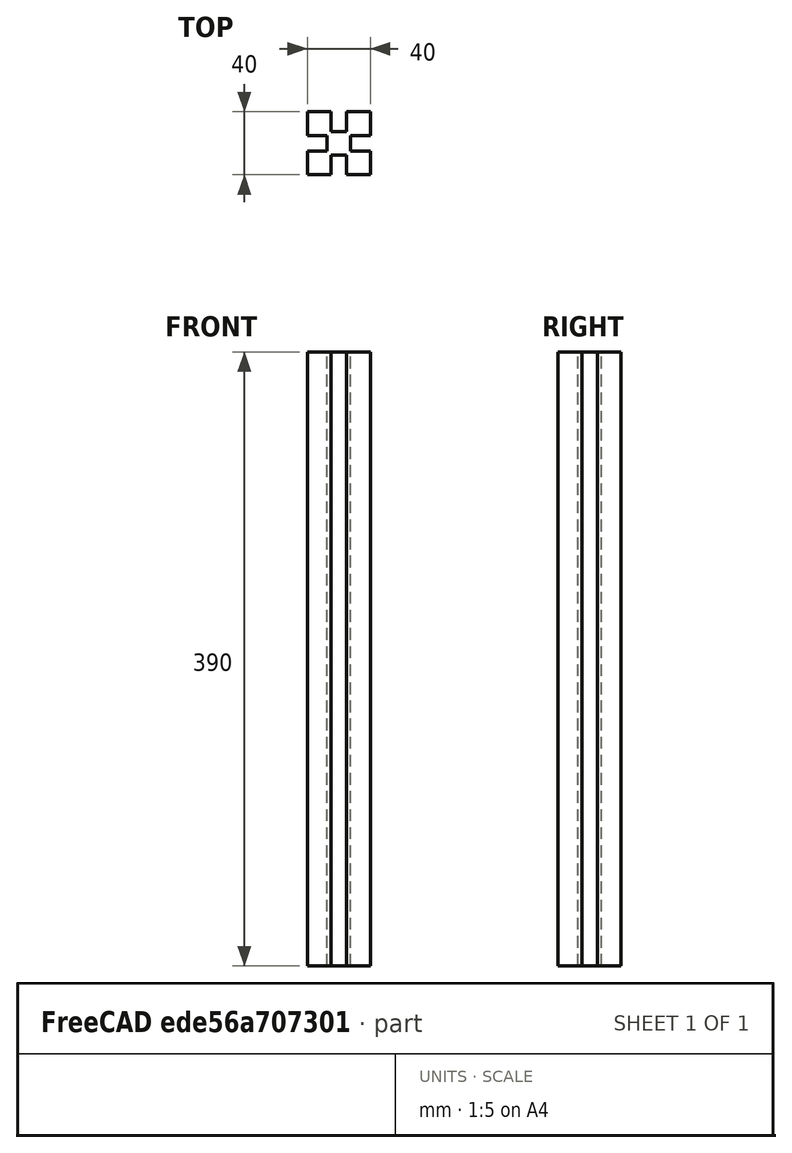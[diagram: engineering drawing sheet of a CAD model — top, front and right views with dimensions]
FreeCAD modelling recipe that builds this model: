
FCSTD DOCUMENT  (FreeCAD 0.18R14555 (Git shallow))
Label: t-slot-profile-390
License: All rights reserved
LicenseURL: http://en.wikipedia.org/wiki/All_rights_reserved
objects: Sketcher::SketchObject×1, PartDesign::Pad×1, PartDesign::Body×1
note: 4 computed .brp shape members not serialized (recipe doc carries the construction recipe); baked Part::Feature solids carry a one-line shape summary decoded from their .brp

FEATURE [Sketcher::SketchObject] Sketch
  MapMode = 5
  Support = -> [XY_Plane]
  sketch-geometry (30):
    g0: LineSegment StartX=-20 StartY=-20 StartZ=0 EndX=-20 EndY=-5 EndZ=0
    g1: LineSegment StartX=-20 StartY=-5 StartZ=0 EndX=-7.5 EndY=-5 EndZ=0
    g2: LineSegment StartX=-7.5 StartY=-5 StartZ=0 EndX=-7.5 EndY=5 EndZ=0
    g3: LineSegment StartX=-7.5 StartY=5 StartZ=0 EndX=-20 EndY=5 EndZ=0
    g4: LineSegment StartX=-20 StartY=5 StartZ=0 EndX=-20 EndY=20 EndZ=0
    g5: LineSegment StartX=-20 StartY=20 StartZ=0 EndX=-5 EndY=20 EndZ=0
    g6: LineSegment StartX=-5 StartY=20 StartZ=0 EndX=-5 EndY=7.5 EndZ=0
    g7: LineSegment StartX=-5 StartY=7.5 StartZ=0 EndX=5 EndY=7.5 EndZ=0
    g8: LineSegment StartX=5 StartY=7.5 StartZ=0 EndX=5 EndY=20 EndZ=0
    g9: LineSegment StartX=5 StartY=20 StartZ=0 EndX=20 EndY=20 EndZ=0
    g10: LineSegment StartX=20 StartY=20 StartZ=0 EndX=20 EndY=5 EndZ=0
    g11: LineSegment StartX=20 StartY=5 StartZ=0 EndX=7.5 EndY=5 EndZ=0
    g12: LineSegment StartX=7.5 StartY=5 StartZ=0 EndX=7.5 EndY=-5 EndZ=0
    g13: LineSegment StartX=7.5 StartY=-5 StartZ=0 EndX=20 EndY=-5 EndZ=0
    g14: LineSegment StartX=20 StartY=-5 StartZ=0 EndX=20 EndY=-20 EndZ=0
    g15: LineSegment StartX=20 StartY=-20 StartZ=0 EndX=5 EndY=-20 EndZ=0
    g16: LineSegment StartX=5 StartY=-20 StartZ=0 EndX=5 EndY=-7.5 EndZ=0
    g17: LineSegment StartX=5 StartY=-7.5 StartZ=0 EndX=-5 EndY=-7.5 EndZ=0
    g18: LineSegment StartX=-5 StartY=-7.5 StartZ=0 EndX=-5 EndY=-20 EndZ=0
    g19: LineSegment StartX=-5 StartY=-20 StartZ=0 EndX=-20 EndY=-20 EndZ=0
    g20: LineSegment [constr] StartX=-5 StartY=-7.5 StartZ=0 EndX=-5 EndY=7.5 EndZ=0
    g21: LineSegment [constr] StartX=5 StartY=7.5 StartZ=0 EndX=5 EndY=-7.5 EndZ=0
    g22: LineSegment [constr] StartX=-7.5 StartY=5 StartZ=0 EndX=7.5 EndY=5 EndZ=0
    g23: LineSegment [constr] StartX=7.5 StartY=-5 StartZ=0 EndX=-7.5 EndY=-5 EndZ=0
    g24: LineSegment [constr] StartX=-20 StartY=-5 StartZ=0 EndX=-20 EndY=5 EndZ=0
    g25: LineSegment [constr] StartX=-5 StartY=20 StartZ=0 EndX=5 EndY=20 EndZ=0
    g26: LineSegment [constr] StartX=20 StartY=5 StartZ=0 EndX=20 EndY=-5 EndZ=0
    g27: LineSegment [constr] StartX=-5 StartY=-20 StartZ=0 EndX=5 EndY=-20 EndZ=0
    g28: LineSegment [constr] StartX=20 StartY=-20 StartZ=0 EndX=-20 EndY=20 EndZ=0
    g29: LineSegment [constr] StartX=-20 StartY=-20 StartZ=0 EndX=20 EndY=20 EndZ=0
  constraints (80):
    c: Vertical(g0)
    c: Coincident(g0,g1)
    c: Horizontal(g1)
    c: Coincident(g1,g2)
    c: Vertical(g2)
    c: Coincident(g2,g3)
    c: Horizontal(g3)
    c: Coincident(g3,g4)
    c: Vertical(g4)
    c: Coincident(g4,g5)
    c: Horizontal(g5)
    c: Coincident(g5,g6)
    c: Vertical(g6)
    c: Coincident(g6,g7)
    c: Horizontal(g7)
    c: Coincident(g7,g8)
    c: Vertical(g8)
    c: Coincident(g8,g9)
    c: Horizontal(g9)
    c: Coincident(g9,g10)
    c: Vertical(g10)
    c: Coincident(g10,g11)
    c: Coincident(g11,g12)
    c: Coincident(g12,g13)
    c: Horizontal(g13)
    c: Coincident(g13,g14)
    c: Vertical(g14)
    c: Coincident(g14,g15)
    c: Horizontal(g15)
    c: Coincident(g15,g16)
    c: Vertical(g16)
    c: Coincident(g16,g17)
    c: Horizontal(g17)
    c: Coincident(g17,g18)
    c: Vertical(g18)
    c: Coincident(g18,g19)
    c: Coincident(g19,g0)
    c: Horizontal(g19)
    c: Horizontal(g11)
    c: Vertical(g12)
    c: Coincident(g20,g17)
    c: Coincident(g20,g6)
    c: Coincident(g21,g7)
    c: Coincident(g21,g16)
    c: Vertical(g21)
    c: Vertical(g20)
    c: Coincident(g22,g2)
    c: Coincident(g22,g11)
    c: Coincident(g23,g12)
    c: Coincident(g23,g1)
    c: Horizontal(g23)
    c: Horizontal(g22)
    c: Coincident(g24,g0)
    c: Coincident(g24,g3)
    c: Vertical(g24)
    c: Coincident(g25,g5)
    c: Coincident(g25,g8)
    c: Horizontal(g25)
    c: Coincident(g26,g10)
    c: Coincident(g26,g13)
    c: Vertical(g26)
    c: Coincident(g27,g18)
    c: Coincident(g27,g15)
    c: Horizontal(g27)
    c: Coincident(g28,g14)
    c: Coincident(g29,g0)
    c: Coincident(g29,g9)
    c: Coincident(g28,g4)
    c: Equal(g0,g19)
    c: Equal(g4,g5)
    c: Equal(g9,g10)
    c: Equal(g2,g7)
    c: Equal(g3,g6)
    c: Equal(g11,g3)
    c: Equal(g1,g18)
    c: DistanceY(g0,g4) = 40
    c: DistanceY(g2,g2) = 10
    c: DistanceY(g18,g18) = 12.5
    c: PointOnObject(g-1,g29)
    c: PointOnObject(g-1,g28)
FEATURE [PartDesign::Pad] Pad
  Length = 390
  Length2 = 100
  Profile = -> Sketch
  Type = 0
FEATURE [PartDesign::Body] Body
  Group = -> [Sketch,Pad]
  Origin = -> Origin
  Tip = -> Pad
